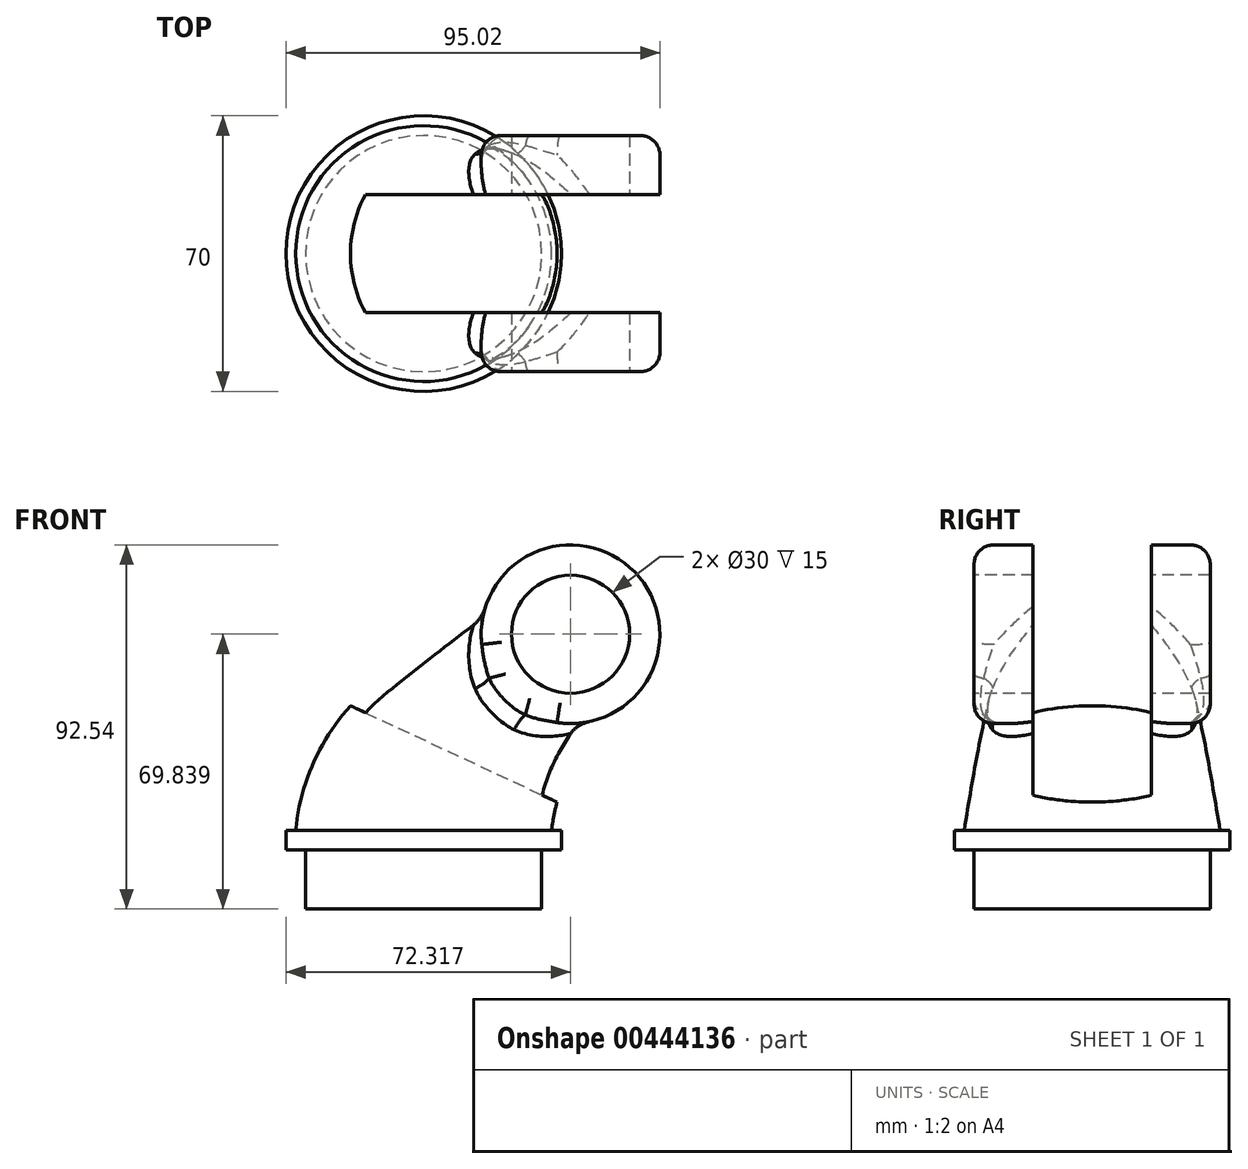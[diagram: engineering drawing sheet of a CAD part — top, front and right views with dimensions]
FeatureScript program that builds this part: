
annotation { "Feature Type Name" : "Feature", "Feature Type Description" : "" }
export const myFeature = defineFeature(function(context is Context, id is Id, definition is map)
    precondition{}
    {
        {
            var Q0;
            Q0=qCreatedBy(makeId("Top.planeOp"),FACE);
            var sketch = newSketch(context, id + "F0", { "sketchPlane" : qUnion([Q0])});
            skCircle(sketch, "E0", {"center": v(0, 0) * mm, "radius": 35 * mm});
            skSolve(sketch);
        }
        {
            var Q0;
            Q0 = qSketchRegion(id + "F0", true);
            extrude(context, id + "F1", {"entities" : qUnion([Q0]), "depth" : 5 * mm});
        }
        {
            var Q0;
            Q0=qCreatedBy(makeId("Front.planeOp"),FACE);
            var sketch = newSketch(context, id + "F2", { "sketchPlane" : qUnion([Q0])});
            skArc(sketch, "E1", {"start": v(17.6, 38.3) * mm, "mid": v(5.55, 23.37) * mm, "end": v(0, 5) * mm});
            skLineSegment(sketch, "E2", {"start": v(17.6, 38.3) * mm, "end": v(35, 52.9) * mm});
            skSolve(sketch);
        }
        {
            var Q0;
            Q0=sQuery(id+"F2.wireOp",EDGE,"E2");
            var Q1;
            Q1=sQuery(id+"F2.wireOp",VERTEX,"E2.end");
            cPlane(context, id + "F3", {"entities" : qUnion([Q0, Q1]), "cplaneType" : CPlaneType.LINE_POINT, "offset" : 25 * mm, "width" : 150 * mm, "height" : 150 * mm});
        }
        {
            var Q0;
            Q0=qCreatedBy(id+"F3.planeOp",FACE);
            var sketch = newSketch(context, id + "F4", { "sketchPlane" : qUnion([Q0])});
            skCircle(sketch, "E3", {"center": v(0, 18.02) * mm, "radius": 22.5 * mm});
            skSolve(sketch);
        }
        {
            var Q0;
            Q0=makeQuery(id+"F1.opExtrude","CAP_FACE",FACE,{"disambiguationData":[OSD([sQuery(id+"F0.wireOp",EDGE,"E0")])],"isStart":false});
            var sketch = newSketch(context, id + "F5", { "sketchPlane" : qUnion([Q0])});
            skCircle(sketch, "E4", {"center": v(0, 0) * mm, "radius": 32.5 * mm});
            skSolve(sketch);
        }
        {
            var Q0;
            Q0=qCreatedBy(makeId("Front.planeOp"),FACE);
            var sketch = newSketch(context, id + "F6", { "sketchPlane" : qUnion([Q0])});
            skArc(sketch, "E5", {"start": v(-13.25, 41.78) * mm, "mid": v(-26.5, 25.3) * mm, "end": v(-32.5, 5) * mm});
            skLineSegment(sketch, "E6", {"start": v(-13.25, 41.78) * mm, "end": v(20.54, 70.13) * mm});
            skSolve(sketch);
        }
        {
            var Q0;
            Q0=qCreatedBy(makeId("Front.planeOp"),FACE);
            var sketch = newSketch(context, id + "F7", { "sketchPlane" : qUnion([Q0])});
            skArc(sketch, "E7", {"start": v(48.46, 34.82) * mm, "mid": v(37.6, 21.45) * mm, "end": v(32.5, 5) * mm});
            skLineSegment(sketch, "E8", {"start": v(48.46, 34.82) * mm, "end": v(49.46, 35.66) * mm});
            skSolve(sketch);
        }
        {
            var Q1;
            Q1=makeQuery(id+"F5.imprint","IMPRINT",FACE,{"disambiguationData":[TD([[makeQuery(id+"F5.imprint","IMPRINT",EDGE,{"derivedFrom":sQuery(id+"F5.wireOp",EDGE,"E4")}),1.0]])]});
            var Q2;
            Q2=makeQuery(id+"F4.imprint","IMPRINT",FACE,{"disambiguationData":[TD([[makeQuery(id+"F4.imprint","IMPRINT",EDGE,{"derivedFrom":sQuery(id+"F4.wireOp",EDGE,"E3")}),1.0]])]});
            var Q3;
            Q3 = qConstructionFilter(qBodyType(qCreatedBy(id + "F7" ,EDGE), BodyType.WIRE), ConstructionObject.NO);
            var Q4;
            Q4 = qConstructionFilter(qBodyType(qCreatedBy(id + "F6" ,EDGE), BodyType.WIRE), ConstructionObject.NO);
            loft(context, id + "F8", {"operationType" : NewBodyOperationType.ADD, "addGuides" : true, "sheetProfilesArray" : [{ "sheetProfileEntities" : qUnion([Q1]) }, { "sheetProfileEntities" : qUnion([Q2]) }], "guidesArray" : [{ "guideEntities" : qUnion([Q3]), "guideDerivativeType" : LoftGuideDerivativeType.DEFAULT, "guideDerivativeMagnitude" : 1 }, { "guideEntities" : qUnion([Q4]), "guideDerivativeType" : LoftGuideDerivativeType.DEFAULT, "guideDerivativeMagnitude" : 1 }]});
        }
        {
            var Q0;
            Q0=qCreatedBy(makeId("Front.planeOp"),FACE);
            var sketch = newSketch(context, id + "F9", { "sketchPlane" : qUnion([Q0])});
            skCircle(sketch, "E9", {"center": v(37.32, 54.84) * mm, "radius": 22.7 * mm});
            skSolve(sketch);
        }
        {
            var Q0;
            Q0 = qSketchRegion(id + "F9", true);
            extrude(context, id + "F10", {"entities" : qUnion([Q0]), "operationType" : NewBodyOperationType.ADD, "endBound" : BoundingType.SYMMETRIC, "depth" : 60 * mm});
        }
        {
            var Q0;
            Q0=makeQuery(id+"F10.boolean.opBoolean","INTERSECT",EDGE,{"derivedFrom":[makeQuery(id+"F8.opLoft","SWEPT_FACE",FACE,{"disambiguationData":[OSD([sQuery(id+"F4.wireOp",EDGE,"E3"),sQuery(id+"F5.wireOp",EDGE,"E4"),sQuery(id+"F6.wireOp",VERTEX,"E6.start"),sQuery(id+"F6.wireOp",EDGE,"E5"),sQuery(id+"F6.wireOp",EDGE,"E6"),sQuery(id+"F7.wireOp",VERTEX,"E8.start"),sQuery(id+"F7.wireOp",EDGE,"E7"),sQuery(id+"F7.wireOp",EDGE,"E8")])]}),makeQuery(id+"F10.opExtrude","SWEPT_FACE",FACE,{"disambiguationData":[OSD([sQuery(id+"F9.wireOp",EDGE,"E9")])]})]});
            fillet(context, id + "F11", {"entities" : qUnion([Q0]), "radius" : 5 * mm, "tangentPropagation" : true, "allowEdgeOverflow" : false});
        }
        {
            var Q0;
            Q0=makeQuery(id+"F10.opExtrude","CAP_FACE",FACE,{"disambiguationData":[OSD([sQuery(id+"F9.wireOp",EDGE,"E9")])],"isStart":false});
            var Q1;
            Q1=makeQuery(id+"F10.opExtrude","CAP_EDGE",EDGE,{"disambiguationData":[OSD([sQuery(id+"F9.wireOp",EDGE,"E9")])],"isStart":true});
            fillet(context, id + "F12", {"entities" : qUnion([Q0, Q1]), "radius" : 5 * mm, "tangentPropagation" : true, "allowEdgeOverflow" : false});
        }
        {
            var Q0;
            Q0=makeQuery(id+"F10.opExtrude","CAP_FACE",FACE,{"disambiguationData":[OSD([sQuery(id+"F9.wireOp",EDGE,"E9")])],"isStart":false});
            var sketch = newSketch(context, id + "F13", { "sketchPlane" : qUnion([Q0])});
            skCircle(sketch, "E10", {"center": v(37.32, 54.84) * mm, "radius": 15 * mm});
            skSolve(sketch);
        }
        {
            var Q0;
            Q0 = qSketchRegion(id + "F13", true);
            extrude(context, id + "F14", {"entities" : qUnion([Q0]), "operationType" : NewBodyOperationType.REMOVE, "endBound" : BoundingType.THROUGH_ALL, "oppositeDirection" : true, "depth" : 25 * mm});
        }
        {
            var Q0;
            Q0=qCreatedBy(makeId("Front.planeOp"),FACE);
            var sketch = newSketch(context, id + "F15", { "sketchPlane" : qUnion([Q0])});
            skLineSegment(sketch, "E11", {"start": v(-106.27, 77.54) * mm, "end": v(60.02, 0) * mm});
            skLineSegment(sketch, "E12", {"start": v(60.02, 77.54) * mm, "end": v(60.02, 0) * mm});
            skLineSegment(sketch, "E13", {"start": v(-106.27, 77.54) * mm, "end": v(60.02, 77.54) * mm});
            skSolve(sketch);
        }
        {
            var Q0;
            Q0 = qSketchRegion(id + "F15", true);
            extrude(context, id + "F16", {"entities" : qUnion([Q0]), "operationType" : NewBodyOperationType.REMOVE, "endBound" : BoundingType.SYMMETRIC, "oppositeDirection" : true, "depth" : 30 * mm});
        }
        {
            var Q0;
            Q0=qCreatedBy(makeId("Front.planeOp"),FACE);
            var sketch = newSketch(context, id + "F17", { "sketchPlane" : qUnion([Q0])});
            skLineSegment(sketch, "E14.bottom", {"start": v(0, 0) * mm, "end": v(-30, 0) * mm});
            skLineSegment(sketch, "E14.top", {"start": v(0, -15) * mm, "end": v(-30, -15) * mm});
            skLineSegment(sketch, "E14.left", {"start": v(0, 0) * mm, "end": v(0, -15) * mm});
            skLineSegment(sketch, "E14.right", {"start": v(-30, 0) * mm, "end": v(-30, -15) * mm});
            skSolve(sketch);
        }
        {
            var Q0;
            Q0=makeQuery(id+"F17.imprint","IMPRINT",FACE,{"disambiguationData":[TD([[makeQuery(id+"F17.imprint","IMPRINT",EDGE,{"derivedFrom":sQuery(id+"F17.wireOp",EDGE,"E14.bottom")}),1.0]])]});
            var Q1;
            Q1=sQuery(id+"F17.wireOp",EDGE,"E14.left");
            revolve(context, id + "F18", {"operationType" : NewBodyOperationType.ADD, "entities" : qUnion([Q0]), "axis" : qUnion([Q1]), "revolveType" : RevolveType.FULL});
        }
    });
